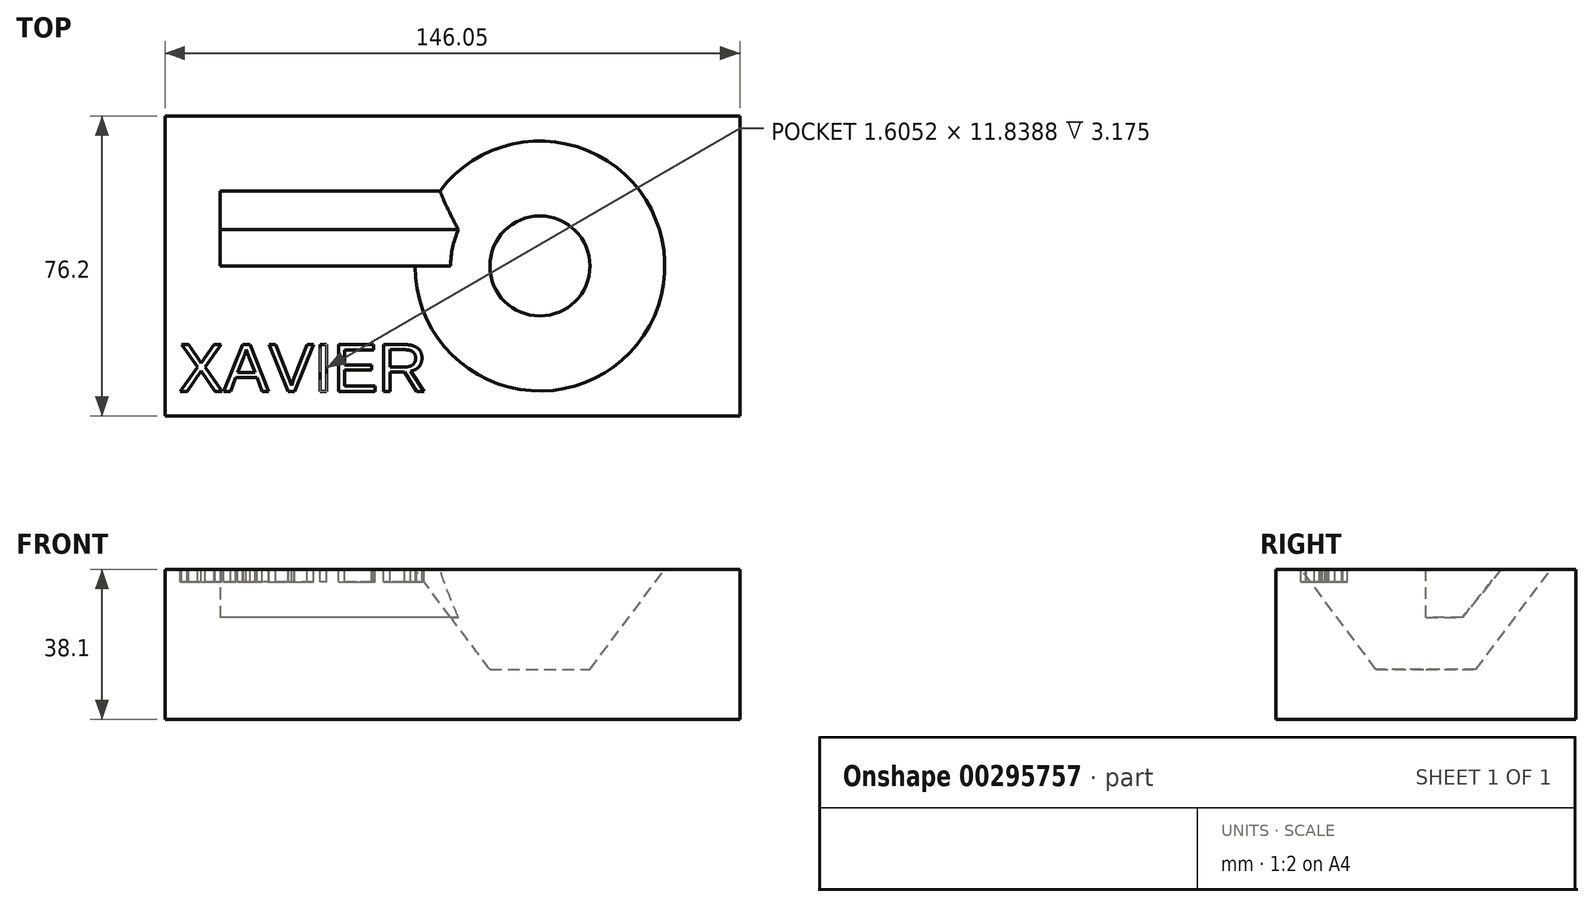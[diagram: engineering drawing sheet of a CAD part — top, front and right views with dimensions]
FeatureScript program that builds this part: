
annotation { "Feature Type Name" : "Feature", "Feature Type Description" : "" }
export const myFeature = defineFeature(function(context is Context, id is Id, definition is map)
    precondition{}
    {
        {
            var Q0;
            Q0=qCreatedBy(makeId("Top.planeOp"),FACE);
            var sketch = newSketch(context, id + "F0", { "sketchPlane" : qUnion([Q0])});
            skLineSegment(sketch, "E0", {"start": v(50.8, -0.34) * mm, "end": v(50.8, 38.1) * mm});
            skLineSegment(sketch, "E1", {"start": v(50.8, 38.1) * mm, "end": v(50.8, -38.1) * mm});
            skLineSegment(sketch, "E2", {"start": v(50.8, -38.1) * mm, "end": v(-95.25, -38.1) * mm});
            skLineSegment(sketch, "E3", {"start": v(-95.25, -38.1) * mm, "end": v(-95.25, 38.1) * mm});
            skLineSegment(sketch, "E4", {"start": v(-95.25, 38.1) * mm, "end": v(50.8, 38.1) * mm});
            skSolve(sketch);
        }
        {
            var Q0;
            {var subQ2=sQuery(id+"F0.wireOp",EDGE,"E2");Q0=makeQuery(id+"F0.imprint","IMPRINT",FACE,{"disambiguationData":[TD([[makeQuery(id+"F0.imprint","IMPRINT",EDGE,{"derivedFrom":subQ2}),-1.0]])]});}
            extrude(context, id + "F1", {"entities" : qUnion([Q0]), "oppositeDirection" : true, "depth" : 38.1 * mm});
        }
        {
            var Q0;
            Q0=qCreatedBy(makeId("Front.planeOp"),FACE);
            var sketch = newSketch(context, id + "F2", { "sketchPlane" : qUnion([Q0])});
            skLineSegment(sketch, "E5", {"start": v(0, 0) * mm, "end": v(-31.75, 0) * mm});
            skLineSegment(sketch, "E6.MirrorCS", {"start": v(-31.75, 0) * mm, "end": v(-12.7, -25.4) * mm});
            skLineSegment(sketch, "E7.MirrorCS", {"start": v(0, -25.4) * mm, "end": v(0, 0) * mm});
            skLineSegment(sketch, "E8.MirrorCS", {"start": v(-12.7, -25.4) * mm, "end": v(0, -25.4) * mm});
            skSolve(sketch);
        }
        {
            var Q0;
            Q0 = qSketchRegion(id + "F2", true);
            var Q1;
            Q1=sQuery(id+"F2.wireOp",EDGE,"E7.MirrorCS");
            revolve(context, id + "F3", {"operationType" : NewBodyOperationType.REMOVE, "entities" : qUnion([Q0]), "axis" : qUnion([Q1]), "revolveType" : RevolveType.FULL});
        }
        {
            var Q0;
            Q0=makeQuery(id+"F1.opExtrude","SWEPT_FACE",FACE,{"disambiguationData":[OSD([sQuery(id+"F0.wireOp",EDGE,"E3")])]});
            var sketch = newSketch(context, id + "F4", { "sketchPlane" : qUnion([Q0])});
            skLineSegment(sketch, "E9", {"start": v(-19.05, 0) * mm, "end": v(0, 0) * mm});
            skLineSegment(sketch, "E10", {"start": v(0, 0) * mm, "end": v(0, -12.13) * mm});
            skLineSegment(sketch, "E11", {"start": v(-19.05, 0) * mm, "end": v(-9.27, -12.13) * mm});
            skLineSegment(sketch, "E12", {"start": v(-9.27, -12.13) * mm, "end": v(0, -12.13) * mm});
            skSolve(sketch);
        }
        {
            var Q0;
            Q0 = qSketchRegion(id + "F4", true);
            extrude(context, id + "F5", {"entities" : qUnion([Q0]), "operationType" : NewBodyOperationType.REMOVE, "oppositeDirection" : true, "depth" : 76.2 * mm});
        }
        {
            var Q0;
            Q0=makeQuery(id+"F1.opExtrude","CAP_FACE",FACE,{"disambiguationData":[OSD([sQuery(id+"F0.wireOp",EDGE,"E1"),sQuery(id+"F0.wireOp",EDGE,"E2"),sQuery(id+"F0.wireOp",EDGE,"E3"),sQuery(id+"F0.wireOp",EDGE,"E4")])],"isStart":true});
            var sketch = newSketch(context, id + "F6", { "sketchPlane" : qUnion([Q0])});
            skLineSegment(sketch, "E13", {"start": v(-91.8, -19.44) * mm, "end": v(-28.3, -19.44) * mm});
            skLineSegment(sketch, "E14", {"start": v(-28.3, -19.44) * mm, "end": v(-28.3, -31.82) * mm});
            skLineSegment(sketch, "E15", {"start": v(-28.3, -31.82) * mm, "end": v(-91.8, -31.82) * mm});
            skLineSegment(sketch, "E16", {"start": v(-91.8, -31.82) * mm, "end": v(-91.8, -19.44) * mm});
            skText(sketch, "E17", { "text": "XAVIER", "fontName": "Arimo-Regular.ttf"});
            const initialGuessF6  = {"E17": [-0.0918, -0.03182, 1, 0, 0.01239]};
            skSetInitialGuess(sketch, initialGuessF6);
            skSolve(sketch);
        }
        {
            var Q0;
            Q0=makeQuery(id+"F6.imprint","IMPRINT",FACE,{"disambiguationData":[TD([[makeQuery(id+"F6.imprint","IMPRINT",EDGE,{"derivedFrom":sQuery(id+"F6.wireOp",EDGE,"E17.sketch_text.stroke-0")}),-1.0]])]});
            var Q1;
            Q1=makeQuery(id+"F6.imprint","IMPRINT",FACE,{"disambiguationData":[TD([[makeQuery(id+"F6.imprint","IMPRINT",EDGE,{"derivedFrom":sQuery(id+"F6.wireOp",EDGE,"E17.sketch_text.stroke-12")}),-1.0]])]});
            var Q2;
            Q2=makeQuery(id+"F6.imprint","IMPRINT",FACE,{"disambiguationData":[TD([[makeQuery(id+"F6.imprint","IMPRINT",EDGE,{"derivedFrom":sQuery(id+"F6.wireOp",EDGE,"E17.sketch_text.stroke-36")}),-1.0]])]});
            var Q3;
            Q3=makeQuery(id+"F6.imprint","IMPRINT",FACE,{"disambiguationData":[TD([[makeQuery(id+"F6.imprint","IMPRINT",EDGE,{"derivedFrom":sQuery(id+"F6.wireOp",EDGE,"E17.sketch_text.stroke-27")}),-1.0]])]});
            var Q4;
            Q4=makeQuery(id+"F6.imprint","IMPRINT",FACE,{"disambiguationData":[TD([[makeQuery(id+"F6.imprint","IMPRINT",EDGE,{"derivedFrom":sQuery(id+"F6.wireOp",EDGE,"E17.sketch_text.stroke-40")}),-1.0]])]});
            var Q5;
            Q5=makeQuery(id+"F6.imprint","IMPRINT",FACE,{"disambiguationData":[TD([[makeQuery(id+"F6.imprint","IMPRINT",EDGE,{"derivedFrom":sQuery(id+"F6.wireOp",EDGE,"E17.sketch_text.stroke-52")}),-1.0]])]});
            extrude(context, id + "F7", {"entities" : qUnion([Q0, Q1, Q2, Q3, Q4, Q5]), "operationType" : NewBodyOperationType.REMOVE, "oppositeDirection" : true, "depth" : 3.17 * mm});
        }
        {
            var Q0;
            Q0=makeQuery(id+"F1.opExtrude","SWEPT_FACE",FACE,{"disambiguationData":[OSD([sQuery(id+"F0.wireOp",EDGE,"E3")])]});
            var sketch = newSketch(context, id + "F8", { "sketchPlane" : qUnion([Q0])});
            skLineSegment(sketch, "E18", {"start": v(-19.05, 0) * mm, "end": v(0, 0) * mm});
            skLineSegment(sketch, "E19", {"start": v(0, 0) * mm, "end": v(0, -12.13) * mm});
            skLineSegment(sketch, "E20", {"start": v(0, -12.13) * mm, "end": v(-9.27, -12.13) * mm});
            skLineSegment(sketch, "E21", {"start": v(-9.27, -12.13) * mm, "end": v(-19.05, 0) * mm});
            skSolve(sketch);
        }
        {
            var Q0;
            Q0 = qSketchRegion(id + "F8", true);
            extrude(context, id + "F9", {"entities" : qUnion([Q0]), "operationType" : NewBodyOperationType.ADD, "oppositeDirection" : true, "depth" : 13.97 * mm});
        }
    });
